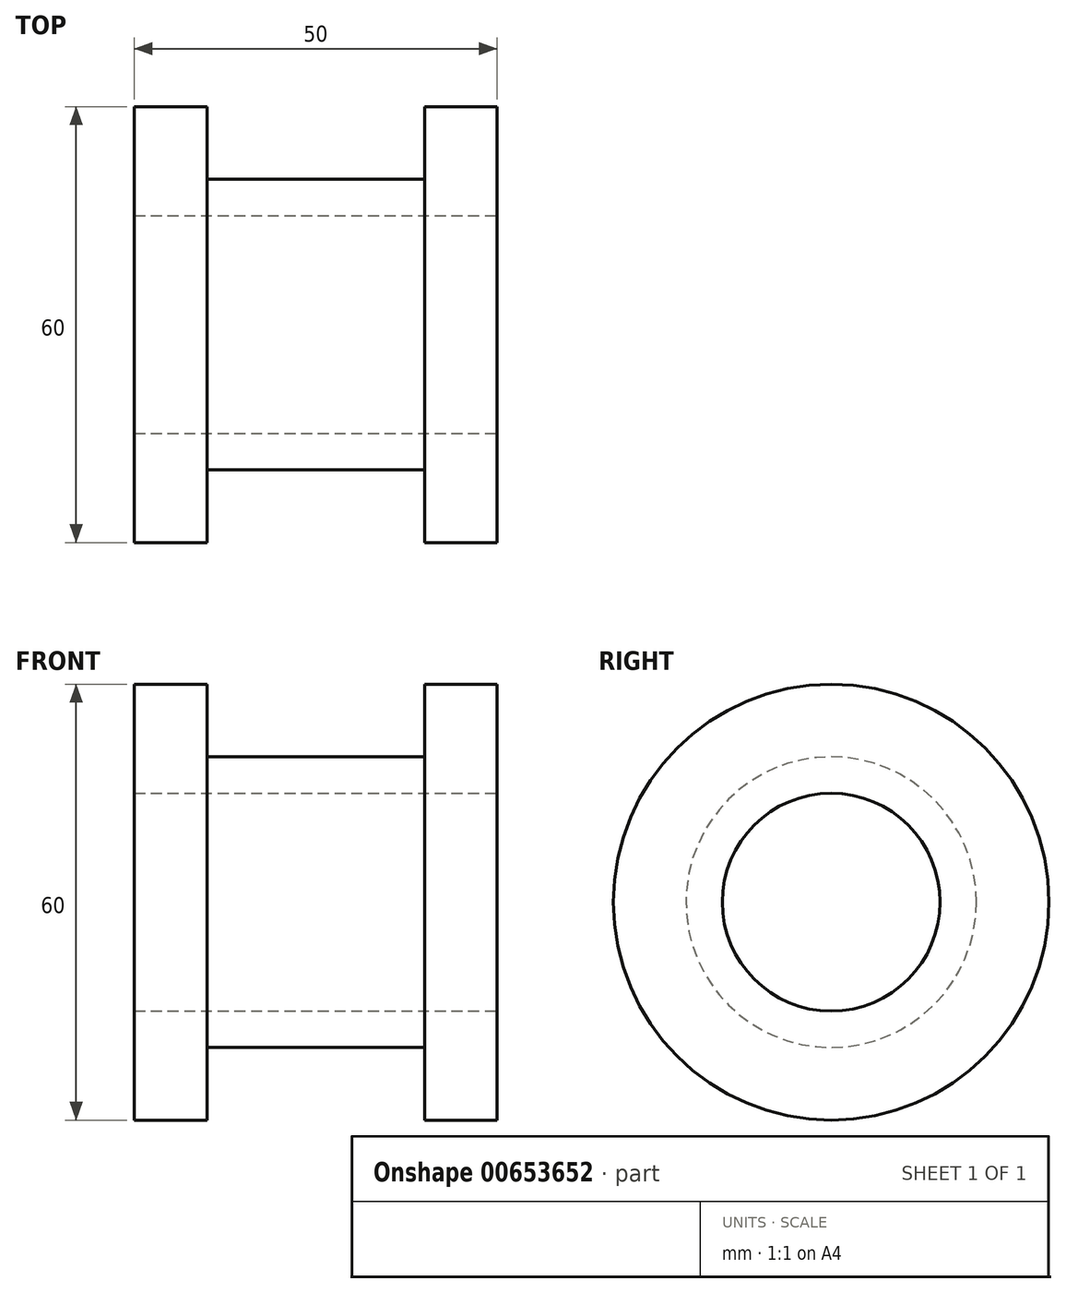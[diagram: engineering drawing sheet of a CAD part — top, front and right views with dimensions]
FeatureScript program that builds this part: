
annotation { "Feature Type Name" : "Feature", "Feature Type Description" : "" }
export const myFeature = defineFeature(function(context is Context, id is Id, definition is map)
    precondition{}
    {
        {
            var Q0;
            Q0=qCreatedBy(makeId("Right.planeOp"),FACE);
            var sketch = newSketch(context, id + "F0", { "sketchPlane" : qUnion([Q0])});
            skCircle(sketch, "E0", {"center": v(0, 0) * mm, "radius": 30 * mm});
            skSolve(sketch);
        }
        {
            var Q0;
            Q0 = qSketchRegion(id + "F0", true);
            extrude(context, id + "F1", {"entities" : qUnion([Q0]), "depth" : 10 * mm, "offsetDistance" : 25 * mm});
        }
        {
            var Q0;
            Q0=makeQuery(id+"F1.opExtrude","CAP_FACE",FACE,{"disambiguationData":[OSD([sQuery(id+"F0.wireOp",EDGE,"E0")])],"isStart":false});
            var sketch = newSketch(context, id + "F2", { "sketchPlane" : qUnion([Q0])});
            skCircle(sketch, "E1", {"center": v(0, 0) * mm, "radius": 20 * mm});
            skSolve(sketch);
        }
        {
            var Q0;
            Q0 = qSketchRegion(id + "F2", true);
            extrude(context, id + "F3", {"entities" : qUnion([Q0]), "operationType" : NewBodyOperationType.ADD, "depth" : 30 * mm, "offsetDistance" : 25 * mm});
        }
        {
            var Q0;
            Q0=makeQuery(id+"F3.opExtrude","CAP_FACE",FACE,{"disambiguationData":[OSD([sQuery(id+"F2.wireOp",EDGE,"E1")])],"isStart":false});
            var sketch = newSketch(context, id + "F4", { "sketchPlane" : qUnion([Q0])});
            skCircle(sketch, "E2", {"center": v(0, 0) * mm, "radius": 30 * mm});
            skSolve(sketch);
        }
        {
            var Q0;
            Q0 = qSketchRegion(id + "F4", true);
            extrude(context, id + "F5", {"entities" : qUnion([Q0]), "operationType" : NewBodyOperationType.ADD, "depth" : 10 * mm, "offsetDistance" : 25 * mm});
        }
        {
            var Q0;
            Q0=makeQuery(id+"F5.opExtrude","CAP_FACE",FACE,{"disambiguationData":[OSD([sQuery(id+"F4.wireOp",EDGE,"E2")])],"isStart":false});
            var sketch = newSketch(context, id + "F6", { "sketchPlane" : qUnion([Q0])});
            skCircle(sketch, "E3", {"center": v(0, 0) * mm, "radius": 15 * mm});
            skSolve(sketch);
        }
        {
            var Q0;
            Q0=makeQuery(id+"F6.imprint","IMPRINT",FACE,{"disambiguationData":[TD([[makeQuery(id+"F6.imprint","IMPRINT",EDGE,{"derivedFrom":sQuery(id+"F6.wireOp",EDGE,"E3")}),1.0]])]});
            extrude(context, id + "F7", {"entities" : qUnion([Q0]), "operationType" : NewBodyOperationType.REMOVE, "endBound" : BoundingType.UP_TO_NEXT, "oppositeDirection" : true, "depth" : 25 * mm, "offsetDistance" : 25 * mm});
        }
    });
